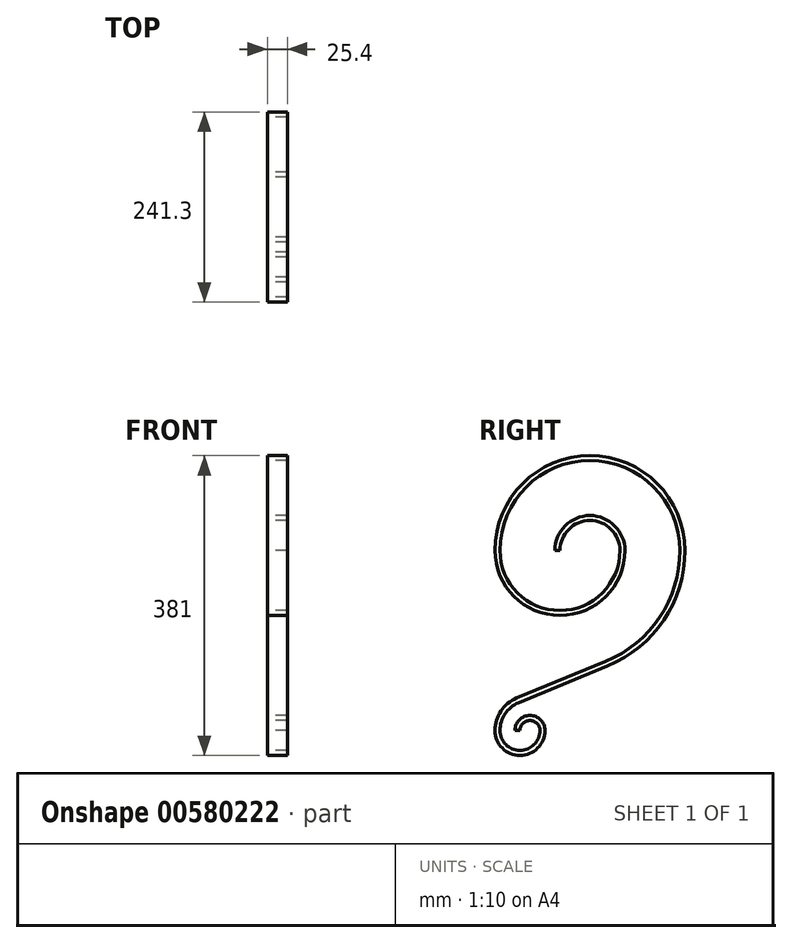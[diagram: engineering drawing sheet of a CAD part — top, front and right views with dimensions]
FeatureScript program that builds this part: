
annotation { "Feature Type Name" : "Feature", "Feature Type Description" : "" }
export const myFeature = defineFeature(function(context is Context, id is Id, definition is map)
    precondition{}
    {
        {
            var Q0;
            Q0=qCreatedBy(makeId("Right.planeOp"),FACE);
            var sketch = newSketch(context, id + "F0", { "sketchPlane" : qUnion([Q0])});
            skArc(sketch, "E0", {"start": v(25.4, 0) * mm, "mid": v(12.7, 12.7) * mm, "end": v(0, 0) * mm});
            skArc(sketch, "E1", {"start": v(-25.4, 0) * mm, "mid": v(0, -25.4) * mm, "end": v(25.4, 0) * mm});
            skArc(sketch, "E2", {"start": v(-1.81, 35.23) * mm, "mid": v(-18.96, 21.2) * mm, "end": v(-25.4, 0) * mm});
            skArc(sketch, "E3.0", {"start": v(31.75, 0) * mm, "mid": v(12.7, 19.05) * mm, "end": v(-6.35, 0) * mm});
            skArc(sketch, "E3.3", {"start": v(-4.23, 41.1) * mm, "mid": v(-24.24, 24.73) * mm, "end": v(-31.75, 0) * mm});
            skArc(sketch, "E3.4", {"start": v(-31.75, 0) * mm, "mid": v(0, -31.75) * mm, "end": v(31.75, 0) * mm});
            skLineSegment(sketch, "E4", {"start": v(-6.35, 0) * mm, "end": v(0, 0) * mm});
            skArc(sketch, "E5", {"start": v(127, 228.6) * mm, "mid": v(88.9, 266.7) * mm, "end": v(50.8, 228.6) * mm});
            skArc(sketch, "E6", {"start": v(-25.4, 228.6) * mm, "mid": v(50.8, 152.4) * mm, "end": v(127, 228.6) * mm});
            skArc(sketch, "E7", {"start": v(203.2, 228.6) * mm, "mid": v(88.9, 342.9) * mm, "end": v(-25.4, 228.6) * mm});
            skArc(sketch, "E8", {"start": v(108.85, 87.7) * mm, "mid": v(177.44, 143.81) * mm, "end": v(203.2, 228.6) * mm});
            skArc(sketch, "E9.0", {"start": v(133.35, 228.6) * mm, "mid": v(88.9, 273.05) * mm, "end": v(44.45, 228.6) * mm});
            skArc(sketch, "E9.1", {"start": v(-31.75, 228.6) * mm, "mid": v(50.8, 146.05) * mm, "end": v(133.35, 228.6) * mm});
            skArc(sketch, "E9.2", {"start": v(209.55, 228.6) * mm, "mid": v(88.9, 349.25) * mm, "end": v(-31.75, 228.6) * mm});
            skArc(sketch, "E9.3", {"start": v(111.27, 81.82) * mm, "mid": v(182.71, 140.28) * mm, "end": v(209.55, 228.6) * mm});
            skLineSegment(sketch, "E10", {"start": v(44.45, 228.6) * mm, "end": v(50.8, 228.6) * mm});
            skLineSegment(sketch, "E11", {"start": v(-4.23, 41.1) * mm, "end": v(108.85, 87.7) * mm});
            skLineSegment(sketch, "E12", {"start": v(-1.81, 35.23) * mm, "end": v(111.27, 81.82) * mm});
            skLineSegment(sketch, "E13", {"start": v(88.9, 349.25) * mm, "end": v(-58.44, 349.25) * mm, "construction": true});
            skLineSegment(sketch, "E14", {"start": v(0, -31.75) * mm, "end": v(-101.38, -31.75) * mm, "construction": true});
            skPoint(sketch, "E14.startSnap0", {"position": v(0, -31.75) * mm});
            skSolve(sketch);
        }
        {
            var Q0;
            Q0=makeQuery(id+"F0.imprint","IMPRINT",FACE,{"disambiguationData":[TD([[makeQuery(id+"F0.imprint","IMPRINT",EDGE,{"derivedFrom":sQuery(id+"F0.wireOp",EDGE,"E0")}),-1.0]])]});
            extrude(context, id + "F1", {"entities" : qUnion([Q0]), "depth" : 25.4 * mm, "offsetDistance" : 25.4 * mm});
        }
    });
